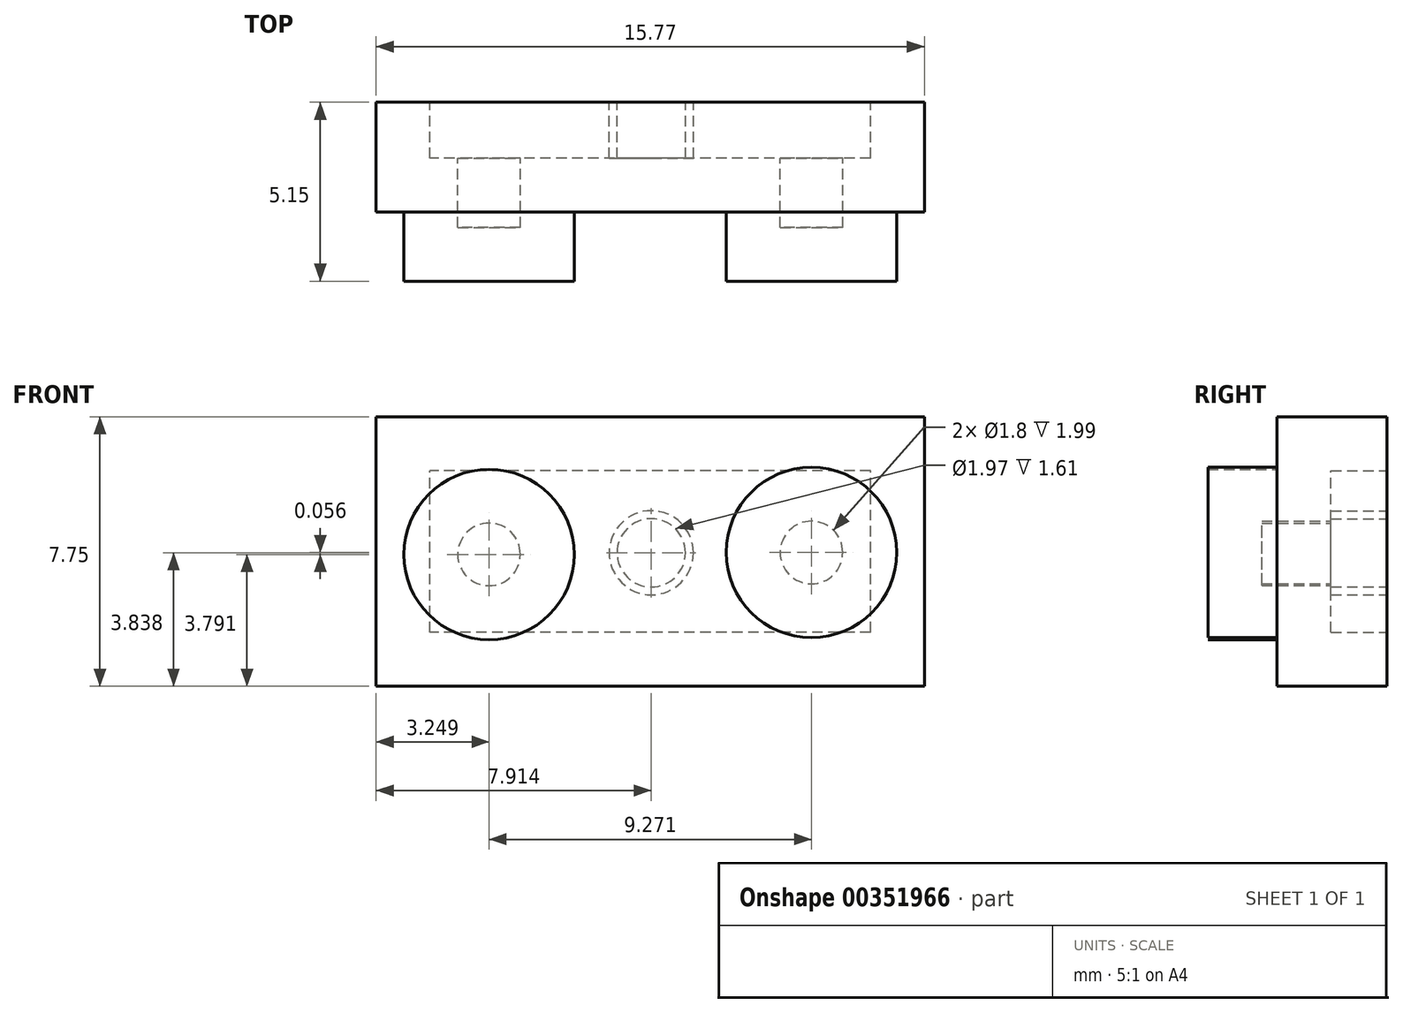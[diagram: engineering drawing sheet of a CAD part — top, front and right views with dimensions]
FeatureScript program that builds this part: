
annotation { "Feature Type Name" : "Feature", "Feature Type Description" : "" }
export const myFeature = defineFeature(function(context is Context, id is Id, definition is map)
    precondition{}
    {
        {
            var Q0;
            Q0=qCreatedBy(makeId("Front.planeOp"),FACE);
            var sketch = newSketch(context, id + "F0", { "sketchPlane" : qUnion([Q0])});
            skLineSegment(sketch, "E0.bottom", {"start": v(0, 0) * mm, "end": v(-15.77, 0) * mm});
            skLineSegment(sketch, "E0.top", {"start": v(0, 7.75) * mm, "end": v(-15.77, 7.75) * mm});
            skLineSegment(sketch, "E0.left", {"start": v(0, 0) * mm, "end": v(0, 7.75) * mm});
            skLineSegment(sketch, "E0.right", {"start": v(-15.77, 0) * mm, "end": v(-15.77, 7.75) * mm});
            skSolve(sketch);
        }
        {
            var Q0;
            Q0 = qSketchRegion(id + "F0", true);
            extrude(context, id + "F1", {"entities" : qUnion([Q0]), "depth" : 3.16 * mm});
        }
        {
            var Q0;
            Q0=makeQuery(id+"F1.opExtrude","CAP_FACE",FACE,{"disambiguationData":[OSD([sQuery(id+"F0.wireOp",EDGE,"E0.bottom"),sQuery(id+"F0.wireOp",EDGE,"E0.top"),sQuery(id+"F0.wireOp",EDGE,"E0.left"),sQuery(id+"F0.wireOp",EDGE,"E0.right")])],"isStart":false});
            var sketch = newSketch(context, id + "F2", { "sketchPlane" : qUnion([Q0])});
            skCircle(sketch, "E1", {"center": v(-12.52, 3.8) * mm, "radius": 2.45 * mm});
            skCircle(sketch, "E2", {"center": v(-3.25, 3.85) * mm, "radius": 2.45 * mm});
            skSolve(sketch);
        }
        {
            var Q0;
            Q0 = qSketchRegion(id + "F2", true);
            extrude(context, id + "F3", {"entities" : qUnion([Q0]), "operationType" : NewBodyOperationType.ADD, "depth" : 1.99 * mm});
        }
        {
            var Q0;
            Q0=makeQuery(id+"F1.opExtrude","CAP_FACE",FACE,{"disambiguationData":[OSD([sQuery(id+"F0.wireOp",EDGE,"E0.bottom"),sQuery(id+"F0.wireOp",EDGE,"E0.top"),sQuery(id+"F0.wireOp",EDGE,"E0.left"),sQuery(id+"F0.wireOp",EDGE,"E0.right")])],"isStart":true});
            shell(context, id + "F4", {"entities" : qUnion([Q0]), "thickness" : 1.55 * mm});
        }
        {
            var Q0;
            Q0=qCreatedBy(makeId("Front.planeOp"),FACE);
            var sketch = newSketch(context, id + "F5", { "sketchPlane" : qUnion([Q0])});
            skCircle(sketch, "E3", {"center": v(-7.86, 3.84) * mm, "radius": 1.2 * mm});
            skCircle(sketch, "E4", {"center": v(-7.86, 3.84) * mm, "radius": 0.98 * mm});
            skSolve(sketch);
        }
        {
            var Q0;
            Q0 = qSketchRegion(id + "F5", true);
            extrude(context, id + "F6", {"entities" : qUnion([Q0]), "operationType" : NewBodyOperationType.ADD, "depth" : 2 * mm});
        }
    });
